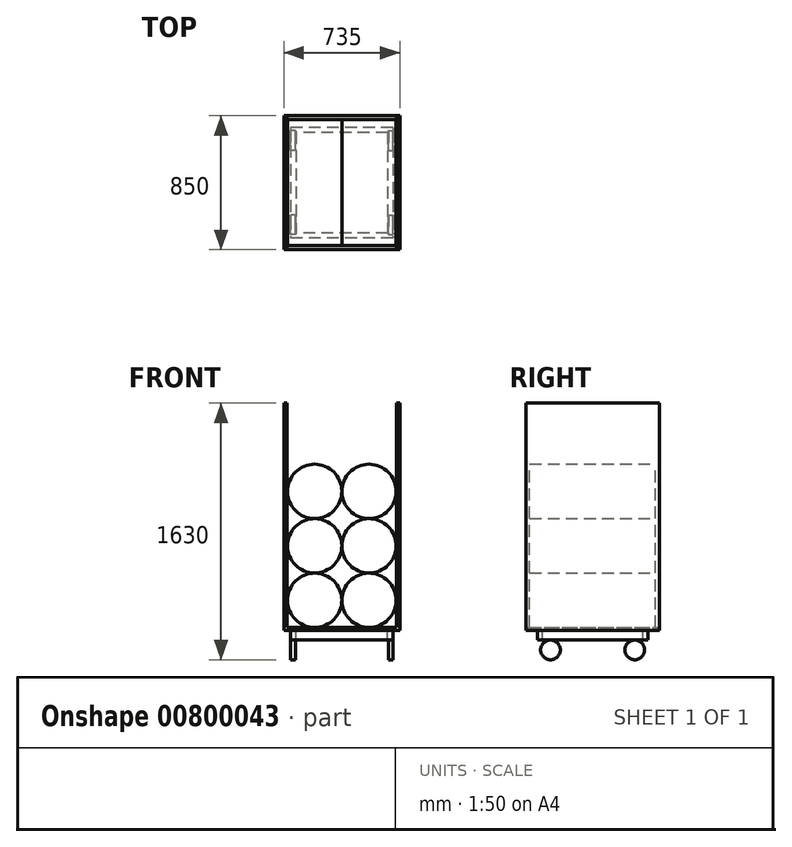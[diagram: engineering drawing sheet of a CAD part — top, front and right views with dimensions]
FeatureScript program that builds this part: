
annotation { "Feature Type Name" : "Feature", "Feature Type Description" : "" }
export const myFeature = defineFeature(function(context is Context, id is Id, definition is map)
    precondition{}
    {
        {
            var Q0;
            Q0=qCreatedBy(makeId("Top.planeOp"),FACE);
            var sketch = newSketch(context, id + "F0", { "sketchPlane" : qUnion([Q0])});
            skLineSegment(sketch, "E0.bottom", {"start": v(367.5, -425) * mm, "end": v(-367.5, -425) * mm});
            skLineSegment(sketch, "E0.top", {"start": v(367.5, 425) * mm, "end": v(-367.5, 425) * mm});
            skLineSegment(sketch, "E0.left", {"start": v(367.5, -425) * mm, "end": v(367.5, 425) * mm});
            skLineSegment(sketch, "E0.right", {"start": v(-367.5, -425) * mm, "end": v(-367.5, 425) * mm});
            skPoint(sketch, "E0.middle", {"position": v(0, 0) * mm});
            skSolve(sketch);
        }
        {
            var Q0;
            Q0=makeQuery(id+"F0.imprint","IMPRINT",FACE,{"disambiguationData":[TD([[makeQuery(id+"F0.imprint","IMPRINT",EDGE,{"derivedFrom":sQuery(id+"F0.wireOp",EDGE,"E0.bottom")}),-1.0]])]});
            extrude(context, id + "F1", {"entities" : qUnion([Q0]), "endBound" : BoundingType.SYMMETRIC, "depth" : 20 * mm, "offsetDistance" : 25 * mm});
        }
        {
            var Q0;
            Q0=makeQuery(id+"F1.opExtrude","CAP_FACE",FACE,{"disambiguationData":[OSD([sQuery(id+"F0.wireOp",EDGE,"E0.bottom"),sQuery(id+"F0.wireOp",EDGE,"E0.top"),sQuery(id+"F0.wireOp",EDGE,"E0.left"),sQuery(id+"F0.wireOp",EDGE,"E0.right")])],"isStart":false});
            var sketch = newSketch(context, id + "F2", { "sketchPlane" : qUnion([Q0])});
            skLineSegment(sketch, "E1.bottom", {"start": v(-367.5, -425) * mm, "end": v(-347.5, -425) * mm});
            skLineSegment(sketch, "E1.top", {"start": v(-367.5, 425) * mm, "end": v(-347.5, 425) * mm});
            skLineSegment(sketch, "E1.left", {"start": v(-367.5, -425) * mm, "end": v(-367.5, 425) * mm});
            skLineSegment(sketch, "E1.right", {"start": v(-347.5, -425) * mm, "end": v(-347.5, 425) * mm});
            skLineSegment(sketch, "E2.bottom", {"start": v(367.5, -425) * mm, "end": v(347.5, -425) * mm});
            skLineSegment(sketch, "E2.top", {"start": v(367.5, 425) * mm, "end": v(347.5, 425) * mm});
            skLineSegment(sketch, "E2.left", {"start": v(367.5, -425) * mm, "end": v(367.5, 425) * mm});
            skLineSegment(sketch, "E2.right", {"start": v(347.5, -425) * mm, "end": v(347.5, 425) * mm});
            skSolve(sketch);
        }
        {
            var Q0;
            Q0 = qSketchRegion(id + "F2", true);
            extrude(context, id + "F3", {"entities" : qUnion([Q0]), "operationType" : NewBodyOperationType.ADD, "depth" : 1425 * mm, "offsetDistance" : 25 * mm});
        }
        {
            var Q0;
            Q0=qCreatedBy(makeId("Front.planeOp"),FACE);
            var sketch = newSketch(context, id + "F4", { "sketchPlane" : qUnion([Q0])});
            skCircle(sketch, "E3", {"center": v(-173, 182.5) * mm, "radius": 172.5 * mm});
            skCircle(sketch, "E4", {"center": v(172, 182.5) * mm, "radius": 172.5 * mm});
            skCircle(sketch, "E5.0.1.0", {"center": v(-173, 528.5) * mm, "radius": 172.5 * mm});
            skCircle(sketch, "E5.0.1.1", {"center": v(172, 528.5) * mm, "radius": 172.5 * mm});
            skCircle(sketch, "E5.0.2.0", {"center": v(-173, 874.5) * mm, "radius": 172.5 * mm});
            skCircle(sketch, "E5.0.2.1", {"center": v(172, 874.5) * mm, "radius": 172.5 * mm});
            skLineSegment(sketch, "E5.direction1", {"start": v(-173, 182.5) * mm, "end": v(-148, 182.5) * mm, "construction": true});
            skLineSegment(sketch, "E5.direction2", {"start": v(-173, 182.5) * mm, "end": v(-173, 528.5) * mm, "construction": true});
            skSolve(sketch);
        }
        {
            var Q0;
            Q0 = qSketchRegion(id + "F4", true);
            extrude(context, id + "F5", {"entities" : qUnion([Q0]), "operationType" : NewBodyOperationType.ADD, "endBound" : BoundingType.SYMMETRIC, "depth" : 800 * mm, "offsetDistance" : 25 * mm});
        }
        {
            var Q0;
            Q0=makeQuery(id+"F1.opExtrude","CAP_FACE",FACE,{"disambiguationData":[OSD([sQuery(id+"F0.wireOp",EDGE,"E0.bottom"),sQuery(id+"F0.wireOp",EDGE,"E0.top"),sQuery(id+"F0.wireOp",EDGE,"E0.left"),sQuery(id+"F0.wireOp",EDGE,"E0.right")])],"isStart":true});
            var sketch = newSketch(context, id + "F6", { "sketchPlane" : qUnion([Q0])});
            skLineSegment(sketch, "E6.bottom", {"start": v(325, -350) * mm, "end": v(-325, -350) * mm});
            skLineSegment(sketch, "E6.top", {"start": v(325, 350) * mm, "end": v(-325, 350) * mm});
            skLineSegment(sketch, "E6.left", {"start": v(325, -350) * mm, "end": v(325, 350) * mm});
            skLineSegment(sketch, "E6.right", {"start": v(-325, -350) * mm, "end": v(-325, 350) * mm});
            skPoint(sketch, "E6.middle", {"position": v(0, 0) * mm});
            skLineSegment(sketch, "E7.bottom", {"start": v(290, -320) * mm, "end": v(-290, -320) * mm});
            skLineSegment(sketch, "E7.top", {"start": v(290, 320) * mm, "end": v(-290, 320) * mm});
            skLineSegment(sketch, "E7.left", {"start": v(290, -320) * mm, "end": v(290, 320) * mm});
            skLineSegment(sketch, "E7.right", {"start": v(-290, -320) * mm, "end": v(-290, 320) * mm});
            skSolve(sketch);
        }
        {
            var Q0;
            Q0 = qSketchRegion(id + "F6", true);
            extrude(context, id + "F7", {"entities" : qUnion([Q0]), "operationType" : NewBodyOperationType.ADD, "depth" : 60 * mm, "offsetDistance" : 25 * mm});
        }
        {
            var Q0;
            Q0=makeQuery(id+"F7.opExtrude","SWEPT_FACE",FACE,{"disambiguationData":[OSD([sQuery(id+"F6.wireOp",EDGE,"E6.left")])]});
            var sketch = newSketch(context, id + "F8", { "sketchPlane" : qUnion([Q0])});
            skCircle(sketch, "E8", {"center": v(-267.5, -132.5) * mm, "radius": 62.5 * mm});
            skCircle(sketch, "E9", {"center": v(267.5, -132.5) * mm, "radius": 62.5 * mm});
            skSolve(sketch);
        }
        {
            var Q0;
            Q0 = qSketchRegion(id + "F8", true);
            extrude(context, id + "F9", {"entities" : qUnion([Q0]), "operationType" : NewBodyOperationType.ADD, "oppositeDirection" : true, "depth" : 30 * mm, "offsetDistance" : 25 * mm});
        }
        {
            var Q0;
            Q0=makeQuery(id+"F7.opExtrude","SWEPT_FACE",FACE,{"disambiguationData":[OSD([sQuery(id+"F6.wireOp",EDGE,"E6.right")])]});
            var sketch = newSketch(context, id + "F10", { "sketchPlane" : qUnion([Q0])});
            skCircle(sketch, "E10", {"center": v(-267.5, -132.5) * mm, "radius": 62.5 * mm});
            skCircle(sketch, "E11", {"center": v(267.5, -132.5) * mm, "radius": 62.5 * mm});
            skSolve(sketch);
        }
        {
            var Q0;
            Q0 = qSketchRegion(id + "F10", true);
            extrude(context, id + "F11", {"entities" : qUnion([Q0]), "oppositeDirection" : true, "depth" : 30 * mm, "offsetDistance" : 25 * mm});
        }
    });
